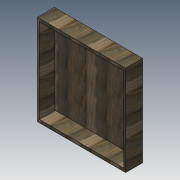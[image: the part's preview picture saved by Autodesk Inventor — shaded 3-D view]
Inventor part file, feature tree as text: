
AUTODESK INVENTOR PART (.ipt)
format: ipt  version: 2018.3 (Build 223284000, 284)  size: 135,680 bytes
history: native  units: in
note: dims shown in document units (in); Inventor stores cm internally (conversion verified against a paired STEP export)
features: extrude x2, sketch x2, projected_geometry x1
ambient origin geometry x8: Origin, YZ Plane, XZ Plane, XY Plane, X Axis, Y Axis, Z Axis, Center Point
bodies: Solid1 (feature_tree)
feature tree (5):
  extrude  "Extrusion1"  Depth=2.11in TaperAngle=0.0deg
  extrude  "Extrusion2"  Depth=0.25in
  sketch  "Sketch1"  dims[d0=11.3386in d2=2.11in d3=0.0in]
  sketch  "Sketch2"  dims[d4=0.175in d5=0.0in d6=0.25in d7=0.25in d8=0.3932in d9=12.125in d10=0.3932in]
  projected_geometry  "Projected Loop1"
